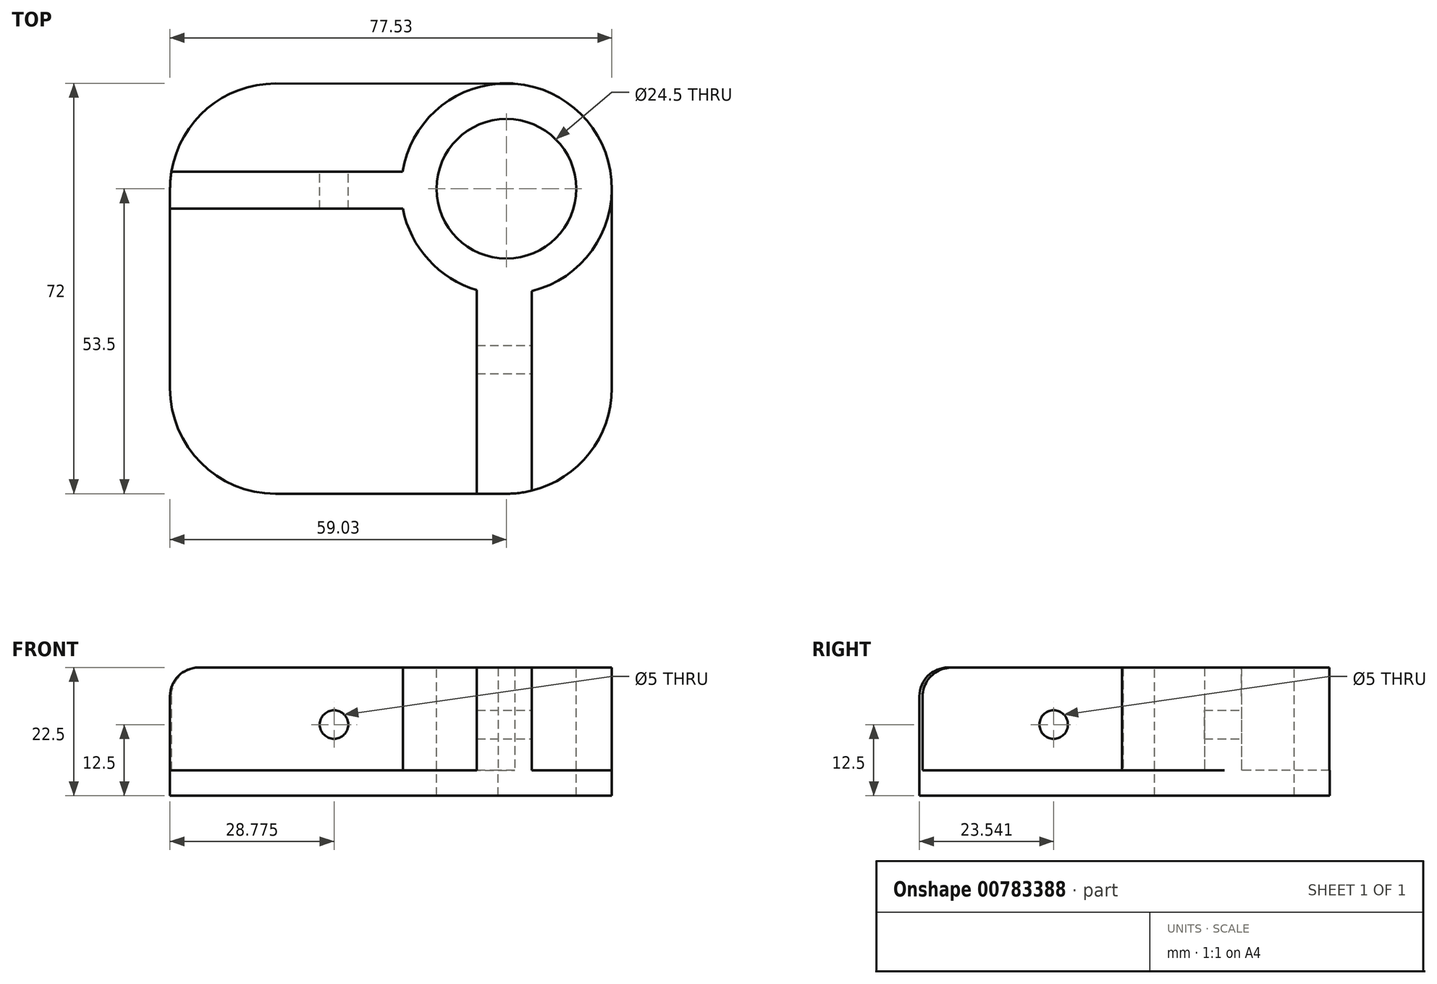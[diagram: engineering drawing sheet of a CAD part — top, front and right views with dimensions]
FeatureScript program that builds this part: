
annotation { "Feature Type Name" : "Feature", "Feature Type Description" : "" }
export const myFeature = defineFeature(function(context is Context, id is Id, definition is map)
    precondition{}
    {
        {
            var Q0;
            Q0=qCreatedBy(makeId("Top.planeOp"),FACE);
            var sketch = newSketch(context, id + "F0", { "sketchPlane" : qUnion([Q0])});
            skLineSegment(sketch, "E0", {"start": v(21, -40) * mm, "end": v(21, -5) * mm});
            skPoint(sketch, "E1.visualSharp", {"position": v(-56.53, 13.48) * mm});
            skPoint(sketch, "E2.visualSharp", {"position": v(-56.53, -58.5) * mm});
            skPoint(sketch, "E3.visualSharp", {"position": v(21, -58.5) * mm});
            skArc(sketch, "E3.filletArc", {"start": v(2.5, -58.5) * mm, "mid": v(15.58, -53.08) * mm, "end": v(21, -40) * mm});
            skLineSegment(sketch, "E4", {"start": v(21, -5) * mm, "end": v(2.5, -5) * mm});
            skCircle(sketch, "E5", {"center": v(2.5, -5) * mm, "radius": 13.35 * mm});
            skCircle(sketch, "E6", {"center": v(2.5, -5) * mm, "radius": 18.5 * mm});
            skLineSegment(sketch, "E7", {"start": v(6.94, -22.96) * mm, "end": v(6.94, -57.96) * mm});
            skLineSegment(sketch, "E8", {"start": v(-2.68, -22.76) * mm, "end": v(-2.68, -58.5) * mm});
            skLineSegment(sketch, "E9", {"start": v(-38.02, 13.47) * mm, "end": v(3.96, 13.44) * mm});
            skLineSegment(sketch, "E10", {"start": v(-56.53, -5.03) * mm, "end": v(-56.53, -40) * mm});
            skLineSegment(sketch, "E11", {"start": v(-38.03, -58.5) * mm, "end": v(2.5, -58.5) * mm});
            skArc(sketch, "E12.filletArc", {"start": v(-38.02, 13.47) * mm, "mid": v(-51.1, 8.06) * mm, "end": v(-56.53, -5.03) * mm});
            skArc(sketch, "E13.filletArc", {"start": v(-56.53, -40) * mm, "mid": v(-51.1, -53.08) * mm, "end": v(-38.03, -58.5) * mm});
            skLineSegment(sketch, "E14", {"start": v(-15.76, -2) * mm, "end": v(-56.28, -2) * mm});
            skLineSegment(sketch, "E15", {"start": v(-15.67, -8.5) * mm, "end": v(-56.53, -8.5) * mm});
            skSolve(sketch);
        }
        {
            var Q0;
            Q0 = qSketchRegion(id + "F0", true);
            extrude(context, id + "F1", {"entities" : qUnion([Q0]), "oppositeDirection" : true, "depth" : 4.5 * mm, "offsetDistance" : 25 * mm});
        }
        {
            var Q0;
            {var subQ4=sQuery(id+"F0.wireOp",EDGE,"E7");Q0=makeQuery(id+"F0.imprint","IMPRINT",FACE,{"disambiguationData":[TD([[makeQuery(id+"F0.imprint","IMPRINT",EDGE,{"derivedFrom":subQ4}),-1.0]])]});}
            var Q1;
            Q1=makeQuery(id+"F0.imprint","IMPRINT",FACE,{"disambiguationData":[TD([[makeQuery(id+"F0.imprint","IMPRINT",EDGE,{"derivedFrom":sQuery(id+"F0.wireOp",EDGE,"E5")}),-1.0]])]});
            var Q2;
            {var subQ3=sQuery(id+"F0.wireOp",EDGE,"E14");Q2=makeQuery(id+"F0.imprint","IMPRINT",FACE,{"disambiguationData":[TD([[makeQuery(id+"F0.imprint","IMPRINT",EDGE,{"derivedFrom":subQ3}),1.0]])]});}
            extrude(context, id + "F2", {"entities" : qUnion([Q0, Q1, Q2]), "operationType" : NewBodyOperationType.ADD, "depth" : 18 * mm, "offsetDistance" : 25 * mm});
        }
        {
            var Q0;
            Q0=makeQuery(id+"F2.opExtrude","SWEPT_FACE",FACE,{"disambiguationData":[OSD([sQuery(id+"F0.wireOp",EDGE,"E7")])]});
            var sketch = newSketch(context, id + "F3", { "sketchPlane" : qUnion([Q0])});
            skLineSegment(sketch, "E16", {"start": v(-22.96, 18) * mm, "end": v(-34.96, 18) * mm});
            skLineSegment(sketch, "E17", {"start": v(-34.96, 18) * mm, "end": v(-34.96, 8) * mm});
            skCircle(sketch, "E18", {"center": v(-34.96, 8) * mm, "radius": 2.5 * mm});
            skSolve(sketch);
        }
        {
            var Q0;
            Q0=makeQuery(id+"F2.opExtrude","SWEPT_FACE",FACE,{"disambiguationData":[OSD([sQuery(id+"F0.wireOp",EDGE,"E14")])]});
            var sketch = newSketch(context, id + "F4", { "sketchPlane" : qUnion([Q0])});
            skLineSegment(sketch, "E19", {"start": v(15.76, 18) * mm, "end": v(27.76, 18) * mm});
            skLineSegment(sketch, "E20", {"start": v(27.76, 18) * mm, "end": v(27.76, 8) * mm});
            skCircle(sketch, "E21", {"center": v(27.76, 8) * mm, "radius": 2.5 * mm});
            skSolve(sketch);
        }
        {
            var Q0;
            Q0=makeQuery(id+"F3.imprint","IMPRINT",FACE,{"disambiguationData":[TD([[makeQuery(id+"F3.imprint","IMPRINT",EDGE,{"derivedFrom":sQuery(id+"F3.wireOp",EDGE,"E18")}),1.0]])]});
            extrude(context, id + "F5", {"entities" : qUnion([Q0]), "operationType" : NewBodyOperationType.REMOVE, "endBound" : BoundingType.THROUGH_ALL, "oppositeDirection" : true, "depth" : 25 * mm, "offsetDistance" : 25 * mm});
        }
        {
            var Q0;
            Q0=makeQuery(id+"F4.imprint","IMPRINT",FACE,{"disambiguationData":[TD([[makeQuery(id+"F4.imprint","IMPRINT",EDGE,{"derivedFrom":sQuery(id+"F4.wireOp",EDGE,"E21")}),1.0]])]});
            extrude(context, id + "F6", {"entities" : qUnion([Q0]), "operationType" : NewBodyOperationType.REMOVE, "endBound" : BoundingType.THROUGH_ALL, "oppositeDirection" : true, "depth" : 25 * mm, "offsetDistance" : 25 * mm});
        }
        {
            var Q0;
            Q0=makeQuery(id+"F2.opExtrude","CAP_EDGE",EDGE,{"disambiguationData":[OSD([sQuery(id+"F0.wireOp",EDGE,"E10")])],"isStart":false});
            var Q1;
            Q1=makeQuery(id+"F2.opExtrude","CAP_EDGE",EDGE,{"disambiguationData":[OSD([sQuery(id+"F0.wireOp",EDGE,"E11")])],"isStart":false});
            var Q2;
            Q2=makeQuery(id+"F2.opExtrude","CAP_EDGE",EDGE,{"disambiguationData":[OSD([sQuery(id+"F0.wireOp",EDGE,"E3.filletArc")])],"isStart":false});
            fillet(context, id + "F7", {"entities" : qUnion([Q0, Q1, Q2]), "radius" : 5 * mm, "tangentPropagation" : true, "allowEdgeOverflow" : false});
        }
        {
            var Q0;
            Q0=makeQuery(id+"F2.opExtrude","CAP_FACE",FACE,{"disambiguationData":[OSD([sQuery(id+"F0.wireOp",EDGE,"E3.filletArc"),sQuery(id+"F0.wireOp",EDGE,"E5"),sQuery(id+"F0.wireOp",EDGE,"E6"),sQuery(id+"F0.wireOp",EDGE,"E7"),sQuery(id+"F0.wireOp",EDGE,"E8"),sQuery(id+"F0.wireOp",EDGE,"E9"),sQuery(id+"F0.wireOp",EDGE,"E10"),sQuery(id+"F0.wireOp",EDGE,"E11"),sQuery(id+"F0.wireOp",EDGE,"E12.filletArc"),sQuery(id+"F0.wireOp",EDGE,"E14"),sQuery(id+"F0.wireOp",EDGE,"E15")])],"isStart":false});
            var sketch = newSketch(context, id + "F8", { "sketchPlane" : qUnion([Q0])});
            skCircle(sketch, "E22.0", {"center": v(2.5, -5) * mm, "radius": 13.35 * mm});
            skCircle(sketch, "E23", {"center": v(2.5, -5) * mm, "radius": 12.25 * mm});
            skSolve(sketch);
        }
        {
            var Q0;
            Q0=makeQuery(id+"F8.imprint","IMPRINT",FACE,{"disambiguationData":[TD([[makeQuery(id+"F8.imprint","IMPRINT",EDGE,{"derivedFrom":sQuery(id+"F8.wireOp",EDGE,"E22.0")}),1.0]])]});
            var Q1;
            Q1=makeQuery(id+"F1.opExtrude","CAP_FACE",FACE,{"disambiguationData":[OSD([sQuery(id+"F0.wireOp",EDGE,"E0"),sQuery(id+"F0.wireOp",EDGE,"E3.filletArc"),sQuery(id+"F0.wireOp",EDGE,"E5"),sQuery(id+"F0.wireOp",EDGE,"E6"),sQuery(id+"F0.wireOp",EDGE,"E9"),sQuery(id+"F0.wireOp",EDGE,"E10"),sQuery(id+"F0.wireOp",EDGE,"E11"),sQuery(id+"F0.wireOp",EDGE,"E12.filletArc"),sQuery(id+"F0.wireOp",EDGE,"E13.filletArc")])],"isStart":false});
            extrude(context, id + "F9", {"entities" : qUnion([Q0]), "operationType" : NewBodyOperationType.ADD, "endBound" : BoundingType.UP_TO_SURFACE, "oppositeDirection" : true, "depth" : 25 * mm, "endBoundEntityFace" : qUnion([Q1]), "offsetDistance" : 25 * mm});
        }
    });
